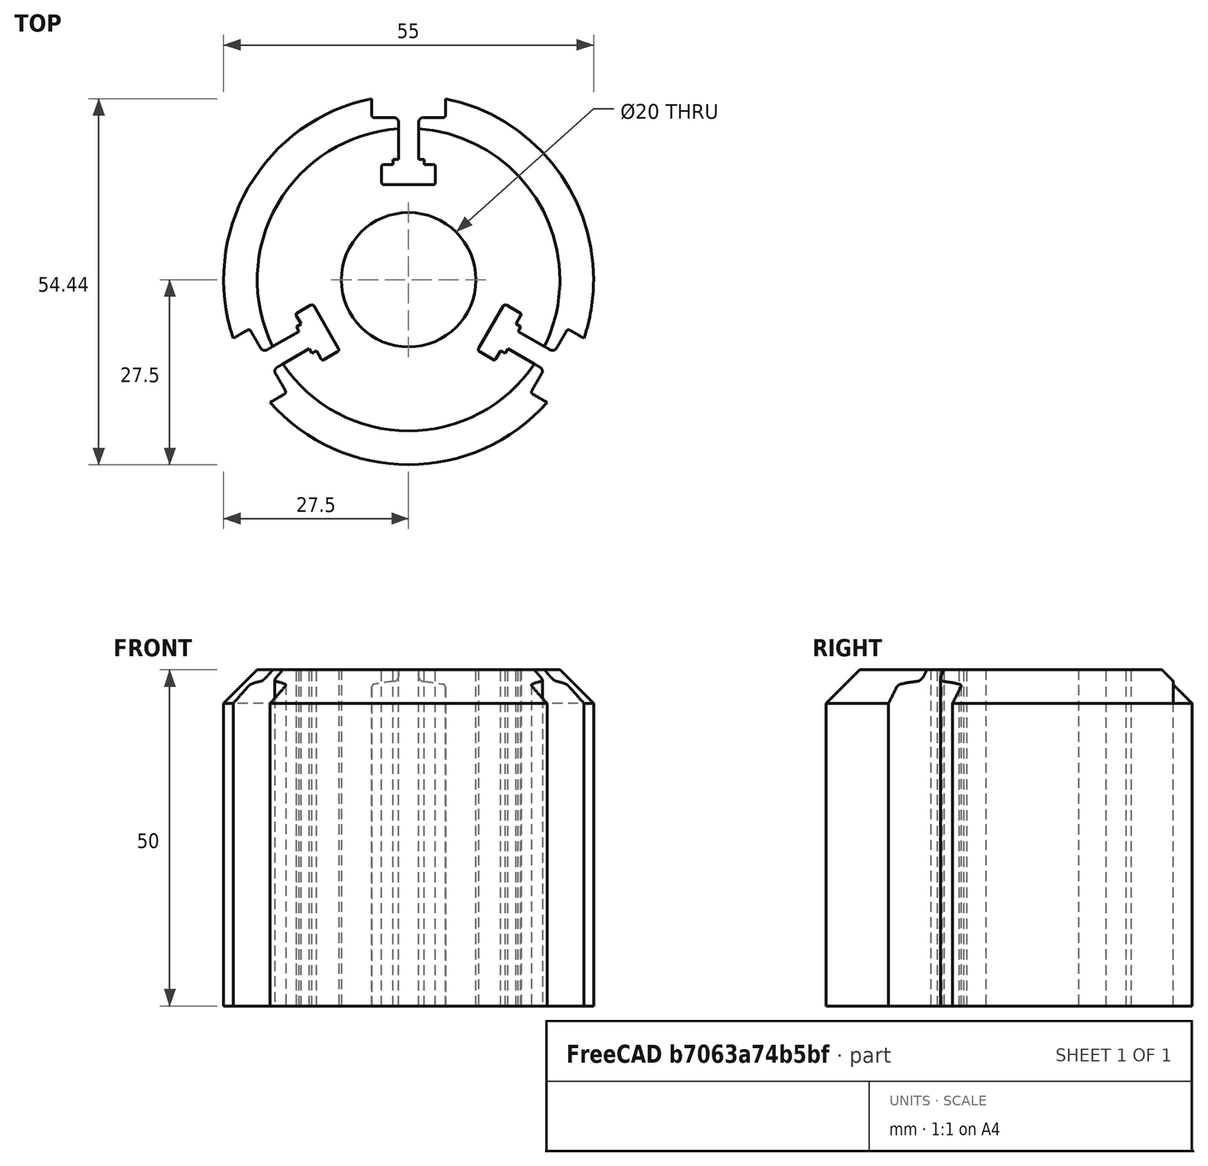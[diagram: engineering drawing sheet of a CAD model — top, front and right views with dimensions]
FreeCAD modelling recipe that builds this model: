
FCSTD DOCUMENT  (FreeCAD 0.21R33771 (Git))
Label: SoportePino
License: All rights reserved
LicenseURL: http://en.wikipedia.org/wiki/All_rights_reserved
objects: Sketcher::SketchObject×2, PartDesign::Pad×1, PartDesign::Chamfer×1, PartDesign::Pocket×1, PartDesign::Body×1
note: 9 computed .brp shape members not serialized (recipe doc carries the construction recipe); baked Part::Feature solids carry a one-line shape summary decoded from their .brp

FEATURE [Sketcher::SketchObject] Sketch
  FullyConstrained = true
  MapMode = 5
  sketch-geometry (2):
    g0: Circle CenterX=0 CenterY=0 CenterZ=0 NormalX=0 NormalY=0 NormalZ=1 AngleXU=0 Radius=27.5
    g1: Circle CenterX=0 CenterY=0 CenterZ=0 NormalX=0 NormalY=0 NormalZ=1 AngleXU=0 Radius=10
  constraints (4):
    c: Diameter(g0) = 55
    c: Coincident(g0,g-1)
    c: Diameter(g1) = 20
    c: Coincident(g1,g0)
FEATURE [PartDesign::Pad] Pad
  Direction = (0,0,1)
  Length = 50
  Length2 = 10
  Profile = -> Sketch
  ReferenceAxis = -> Sketch [N_Axis]
  Type = 0
FEATURE [PartDesign::Chamfer] Chamfer
  Angle = 45
  Base = -> Pad [Edge3]
  BaseFeature = -> Pad
  ChamferType = 0
  FlipDirection = false
  Size = 5
  Size2 = 1
  SupportTransform = false
  UseAllEdges = false
FEATURE [Sketcher::SketchObject] Sketch001
  FullyConstrained = false
  MapMode = 5
  Placement = pos=(0,0,0) rot=(1,0,0;3.14159rad)
  sketch-geometry (108):
    g0: LineSegment StartX=5.5 StartY=-27.8836 StartZ=0 EndX=5.5 EndY=-24.5112 EndZ=0
    g1: LineSegment StartX=5.10884 StartY=-24.12 StartZ=0 EndX=2.18624 EndY=-24.12 EndZ=0
    g2: LineSegment StartX=-1e-16 StartY=-24.12 StartZ=0 EndX=1.5 EndY=-24.12 EndZ=0
    g3: LineSegment StartX=1.5 StartY=-23.4338 StartZ=0 EndX=1.5 EndY=-17.927 EndZ=0
    g4: LineSegment StartX=4 StartY=-16.8721 StartZ=0 EndX=4 EndY=-14.489 EndZ=0
    g5: ArcOfCircle CenterX=2.18624 CenterY=-23.4338 CenterZ=0 NormalX=0 NormalY=0 NormalZ=1 AngleXU=0 Radius=0.686238 StartAngle=3.14159 EndAngle=4.71239
    g6: GeomPoint X=1.5 Y=-17.12 Z=0
    g7: ArcOfCircle CenterX=3.63103 CenterY=-14.489 CenterZ=0 NormalX=0 NormalY=0 NormalZ=1 AngleXU=0 Radius=0.368966 StartAngle=0 EndAngle=1.5708
    g8: GeomPoint X=4 Y=-14.12 Z=0
    g9: ArcOfCircle CenterX=3.75214 CenterY=-16.8721 CenterZ=0 NormalX=0 NormalY=0 NormalZ=1 AngleXU=0 Radius=0.247857 StartAngle=4.71239 EndAngle=6.28319
    g10: GeomPoint X=4 Y=-17.12 Z=0
    g11: ArcOfCircle CenterX=5.10884 CenterY=-24.5112 CenterZ=0 NormalX=0 NormalY=0 NormalZ=1 AngleXU=0 Radius=0.391159 StartAngle=0 EndAngle=1.5708
    g12: GeomPoint X=5.5 Y=-24.12 Z=0
    g13: LineSegment StartX=0 StartY=-25.1224 StartZ=0 EndX=1.5 EndY=-25.1224 EndZ=0
    g14: LineSegment StartX=2.29402 StartY=-17.927 StartZ=0 EndX=2.29402 EndY=-17.12 EndZ=0
    g15: LineSegment StartX=-5.5 StartY=-27.8836 StartZ=0 EndX=-5.5 EndY=-24.5112 EndZ=0
    g16: LineSegment StartX=-5.10884 StartY=-24.12 StartZ=0 EndX=-2.18624 EndY=-24.12 EndZ=0
    g17: LineSegment StartX=1e-16 StartY=-24.12 StartZ=0 EndX=-1.5 EndY=-24.12 EndZ=0
    g18: LineSegment StartX=-1.5 StartY=-23.4338 StartZ=0 EndX=-1.5 EndY=-17.927 EndZ=0
    g19: LineSegment StartX=-4 StartY=-16.8721 StartZ=0 EndX=-4 EndY=-14.489 EndZ=0
    g20: ArcOfCircle CenterX=-2.18624 CenterY=-23.4338 CenterZ=0 NormalX=0 NormalY=0 NormalZ=1 AngleXU=0 Radius=0.686238 StartAngle=4.71239 EndAngle=6.28319
    g21: GeomPoint X=-1.5 Y=-17.12 Z=0
    g22: ArcOfCircle CenterX=-3.63103 CenterY=-14.489 CenterZ=0 NormalX=0 NormalY=0 NormalZ=1 AngleXU=0 Radius=0.368966 StartAngle=1.5708 EndAngle=3.14159
    g23: GeomPoint X=-4 Y=-14.12 Z=0
    g24: ArcOfCircle CenterX=-3.75214 CenterY=-16.8721 CenterZ=0 NormalX=0 NormalY=0 NormalZ=1 AngleXU=0 Radius=0.247857 StartAngle=3.14159 EndAngle=4.71239
    g25: GeomPoint X=-4 Y=-17.12 Z=0
    g26: ArcOfCircle CenterX=-5.10884 CenterY=-24.5112 CenterZ=0 NormalX=0 NormalY=0 NormalZ=1 AngleXU=0 Radius=0.391159 StartAngle=1.5708 EndAngle=3.14159
    g27: GeomPoint X=-5.5 Y=-24.12 Z=0
    g28: LineSegment StartX=0 StartY=-25.1224 StartZ=0 EndX=-1.5 EndY=-25.1224 EndZ=0
    g29: LineSegment StartX=-2.29402 StartY=-17.927 StartZ=0 EndX=-2.29402 EndY=-17.12 EndZ=0
    g30: LineSegment StartX=-5.5 StartY=-27.8836 StartZ=0 EndX=5.5 EndY=-27.8836 EndZ=0
    g31: LineSegment StartX=-2.29402 StartY=-17.927 StartZ=0 EndX=-1.5 EndY=-17.927 EndZ=0
    g32: LineSegment StartX=1.5 StartY=-17.927 StartZ=0 EndX=2.29402 EndY=-17.927 EndZ=0
    g33: LineSegment StartX=-3.75214 StartY=-17.12 StartZ=0 EndX=-2.29402 EndY=-17.12 EndZ=0
    g34: LineSegment StartX=2.29402 StartY=-17.12 StartZ=0 EndX=3.75214 EndY=-17.12 EndZ=0
    g35: LineSegment StartX=3.63103 StartY=-14.12 StartZ=0 EndX=-3.63103 EndY=-14.12 EndZ=0
    g36: LineSegment StartX=21.3979 StartY=18.7049 StartZ=0 EndX=18.4773 EndY=17.0187 EndZ=0
    g37: LineSegment StartX=18.3341 StartY=16.4844 StartZ=0 EndX=19.7954 EndY=13.9533 EndZ=0
    g38: LineSegment StartX=20.8885 StartY=12.06 StartZ=0 EndX=20.1385 EndY=13.359 EndZ=0
    g39: LineSegment StartX=19.5442 StartY=13.0159 StartZ=0 EndX=14.7752 EndY=10.2625 EndZ=0
    g40: LineSegment StartX=12.6117 StartY=11.9002 StartZ=0 EndX=10.5478 EndY=10.7086 EndZ=0
    g41: ArcOfCircle CenterX=19.2011 CenterY=13.6102 CenterZ=0 NormalX=0 NormalY=0 NormalZ=1 AngleXU=0 Radius=0.686238 StartAngle=5.23599 EndAngle=6.80678
    g42: GeomPoint X=14.0764 Y=9.85904 Z=0
    g43: ArcOfCircle CenterX=10.7323 CenterY=10.3891 CenterZ=0 NormalX=0 NormalY=0 NormalZ=1 AngleXU=0 Radius=0.368966 StartAngle=2.0944 EndAngle=3.66519
    g44: GeomPoint X=10.2283 Y=10.5241 Z=0
    g45: ArcOfCircle CenterX=12.7356 CenterY=11.6855 CenterZ=0 NormalX=0 NormalY=0 NormalZ=1 AngleXU=0 Radius=0.247857 StartAngle=0.523599 EndAngle=2.0944
    g46: GeomPoint X=12.8264 Y=12.0241 Z=0
    g47: ArcOfCircle CenterX=18.6729 CenterY=16.68 CenterZ=0 NormalX=0 NormalY=0 NormalZ=1 AngleXU=0 Radius=0.391159 StartAngle=2.09439 EndAngle=3.66519
    g48: GeomPoint X=18.1385 Y=16.8231 Z=0
    g49: LineSegment StartX=21.7567 StartY=12.5612 StartZ=0 EndX=21.0067 EndY=13.8603 EndZ=0
    g50: LineSegment StartX=14.3782 StartY=10.9502 StartZ=0 EndX=13.6793 EndY=10.5467 EndZ=0
    g51: LineSegment StartX=26.8979 StartY=9.17865 StartZ=0 EndX=23.9773 EndY=7.49244 EndZ=0
    g52: LineSegment StartX=23.443 StartY=7.63561 StartZ=0 EndX=21.9817 EndY=10.1667 EndZ=0
    g53: LineSegment StartX=20.8885 StartY=12.06 StartZ=0 EndX=21.6385 EndY=10.761 EndZ=0
    g54: LineSegment StartX=21.0442 StartY=10.4178 StartZ=0 EndX=16.2752 EndY=7.66444 EndZ=0
    g55: LineSegment StartX=16.6117 StartY=4.97197 StartZ=0 EndX=14.5478 EndY=3.78038 EndZ=0
    g56: ArcOfCircle CenterX=21.3874 CenterY=9.82354 CenterZ=0 NormalX=0 NormalY=0 NormalZ=1 AngleXU=0 Radius=0.686238 StartAngle=0.523599 EndAngle=2.0944
    g57: GeomPoint X=15.5764 Y=7.26096 Z=0
    g58: ArcOfCircle CenterX=14.3633 CenterY=4.09992 CenterZ=0 NormalX=0 NormalY=0 NormalZ=1 AngleXU=0 Radius=0.368966 StartAngle=3.66519 EndAngle=5.23599
    g59: GeomPoint X=14.2283 Y=3.5959 Z=0
    g60: ArcOfCircle CenterX=16.4878 CenterY=5.18662 CenterZ=0 NormalX=0 NormalY=0 NormalZ=1 AngleXU=0 Radius=0.247857 StartAngle=5.23599 EndAngle=6.80678
    g61: GeomPoint X=16.8264 Y=5.0959 Z=0
    g62: ArcOfCircle CenterX=23.7817 CenterY=7.83119 CenterZ=0 NormalX=0 NormalY=0 NormalZ=1 AngleXU=0 Radius=0.391159 StartAngle=3.66519 EndAngle=5.23599
    g63: GeomPoint X=23.6385 Y=7.29686 Z=0
    g64: LineSegment StartX=21.7567 StartY=12.5612 StartZ=0 EndX=22.5067 EndY=11.2622 EndZ=0
    g65: LineSegment StartX=16.6722 StartY=6.9768 StartZ=0 EndX=15.9734 EndY=6.57332 EndZ=0
    g66: LineSegment StartX=26.8979 StartY=9.17865 StartZ=0 EndX=21.3979 EndY=18.7049 EndZ=0
    g67: LineSegment StartX=16.6722 StartY=6.9768 StartZ=0 EndX=16.2752 EndY=7.66444 EndZ=0
    g68: LineSegment StartX=14.7752 StartY=10.2625 StartZ=0 EndX=14.3782 EndY=10.9502 EndZ=0
    g69: LineSegment StartX=16.7024 StartY=5.31055 StartZ=0 EndX=15.9734 EndY=6.57332 EndZ=0
    g70: LineSegment StartX=13.6793 StartY=10.5467 StartZ=0 EndX=12.9503 EndY=11.8095 EndZ=0
    g71: LineSegment StartX=10.4128 StartY=10.2046 StartZ=0 EndX=14.0438 EndY=3.91543 EndZ=0
    g72: LineSegment StartX=-26.8979 StartY=9.17865 StartZ=0 EndX=-23.9773 EndY=7.49244 EndZ=0
    g73: LineSegment StartX=-23.443 StartY=7.63561 StartZ=0 EndX=-21.9817 EndY=10.1667 EndZ=0
    g74: LineSegment StartX=-20.8885 StartY=12.06 StartZ=0 EndX=-21.6385 EndY=10.761 EndZ=0
    g75: LineSegment StartX=-21.0442 StartY=10.4178 StartZ=0 EndX=-16.2752 EndY=7.66444 EndZ=0
    g76: LineSegment StartX=-16.6117 StartY=4.97197 StartZ=0 EndX=-14.5478 EndY=3.78038 EndZ=0
    g77: ArcOfCircle CenterX=-21.3874 CenterY=9.82354 CenterZ=0 NormalX=0 NormalY=0 NormalZ=1 AngleXU=0 Radius=0.686238 StartAngle=1.0472 EndAngle=2.61799
    g78: GeomPoint X=-15.5764 Y=7.26096 Z=0
    g79: ArcOfCircle CenterX=-14.3633 CenterY=4.09992 CenterZ=0 NormalX=0 NormalY=0 NormalZ=1 AngleXU=0 Radius=0.368966 StartAngle=4.18879 EndAngle=5.75959
    g80: GeomPoint X=-14.2283 Y=3.5959 Z=0
    g81: ArcOfCircle CenterX=-16.4878 CenterY=5.18662 CenterZ=0 NormalX=0 NormalY=0 NormalZ=1 AngleXU=0 Radius=0.247857 StartAngle=2.61799 EndAngle=4.18879
    g82: GeomPoint X=-16.8264 Y=5.0959 Z=0
    g83: ArcOfCircle CenterX=-23.7817 CenterY=7.83119 CenterZ=0 NormalX=0 NormalY=0 NormalZ=1 AngleXU=0 Radius=0.391159 StartAngle=4.18879 EndAngle=5.75959
    g84: GeomPoint X=-23.6385 Y=7.29686 Z=0
    g85: LineSegment StartX=-21.7567 StartY=12.5612 StartZ=0 EndX=-22.5067 EndY=11.2622 EndZ=0
    g86: LineSegment StartX=-16.6722 StartY=6.9768 StartZ=0 EndX=-15.9734 EndY=6.57332 EndZ=0
    g87: LineSegment StartX=-21.3979 StartY=18.7049 StartZ=0 EndX=-18.4773 EndY=17.0187 EndZ=0
    g88: LineSegment StartX=-18.3341 StartY=16.4844 StartZ=0 EndX=-19.7954 EndY=13.9533 EndZ=0
    g89: LineSegment StartX=-20.8885 StartY=12.06 StartZ=0 EndX=-20.1385 EndY=13.359 EndZ=0
    g90: LineSegment StartX=-19.5442 StartY=13.0159 StartZ=0 EndX=-14.7752 EndY=10.2625 EndZ=0
    g91: LineSegment StartX=-12.6117 StartY=11.9002 StartZ=0 EndX=-10.5478 EndY=10.7086 EndZ=0
    g92: ArcOfCircle CenterX=-19.2011 CenterY=13.6102 CenterZ=0 NormalX=0 NormalY=0 NormalZ=1 AngleXU=0 Radius=0.686238 StartAngle=2.61799 EndAngle=4.18879
    g93: GeomPoint X=-14.0764 Y=9.85904 Z=0
    g94: ArcOfCircle CenterX=-10.7323 CenterY=10.3891 CenterZ=0 NormalX=0 NormalY=0 NormalZ=1 AngleXU=0 Radius=0.368966 StartAngle=5.75959 EndAngle=7.33038
    g95: GeomPoint X=-10.2283 Y=10.5241 Z=0
    g96: ArcOfCircle CenterX=-12.7356 CenterY=11.6855 CenterZ=0 NormalX=0 NormalY=0 NormalZ=1 AngleXU=0 Radius=0.247857 StartAngle=1.0472 EndAngle=2.61799
    g97: GeomPoint X=-12.8264 Y=12.0241 Z=0
    g98: ArcOfCircle CenterX=-18.6729 CenterY=16.68 CenterZ=0 NormalX=0 NormalY=0 NormalZ=1 AngleXU=0 Radius=0.391159 StartAngle=5.75959 EndAngle=7.33038
    g99: GeomPoint X=-18.1385 Y=16.8231 Z=0
    g100: LineSegment StartX=-21.7567 StartY=12.5612 StartZ=0 EndX=-21.0067 EndY=13.8603 EndZ=0
    g101: LineSegment StartX=-14.3782 StartY=10.9502 StartZ=0 EndX=-13.6793 EndY=10.5467 EndZ=0
    g102: LineSegment StartX=-21.3979 StartY=18.7049 StartZ=0 EndX=-26.8979 EndY=9.17865 EndZ=0
    g103: LineSegment StartX=-14.3782 StartY=10.9502 StartZ=0 EndX=-14.7752 EndY=10.2625 EndZ=0
    g104: LineSegment StartX=-16.2752 StartY=7.66444 StartZ=0 EndX=-16.6722 EndY=6.9768 EndZ=0
    g105: LineSegment StartX=-12.9503 StartY=11.8095 StartZ=0 EndX=-13.6793 EndY=10.5467 EndZ=0
    g106: LineSegment StartX=-15.9734 StartY=6.57332 StartZ=0 EndX=-16.7024 EndY=5.31055 EndZ=0
    g107: LineSegment StartX=-14.0438 StartY=3.91543 StartZ=0 EndX=-10.4128 EndY=10.2046 EndZ=0
  constraints (128):
    c: Horizontal(g1)
    c: Vertical(g0)
    c: Horizontal(g2)
    c: Vertical(g3)
    c: Vertical(g4)
    c: Distance(g10,g8) = 3
    c: Tangent(g3,g5) = 1.5708
    c: Tangent(g1,g5) = 1.5708
    c: PointOnObject(g6,g3)
    c: PointOnObject(g8,g4)
    c: Tangent(g4,g7) = -1.5708
    c: PointOnObject(g10,g4)
    c: Tangent(g4,g9) = -1.5708
    c: PointOnObject(g12,g1)
    c: PointOnObject(g12,g0)
    c: Tangent(g1,g11) = -1.5708
    c: Tangent(g0,g11) = -1.5708
    c: Horizontal(g13)
    c: Vertical(g14)
    c: Horizontal(g16)
    c: Vertical(g15)
    c: Horizontal(g17)
    c: Vertical(g18)
    c: Vertical(g19)
    c: Distance(g25,g23) = 3
    c: Tangent(g18,g20) = -1.5708
    c: Tangent(g16,g20) = -1.5708
    c: PointOnObject(g21,g18)
    c: PointOnObject(g23,g19)
    c: Tangent(g19,g22) = 1.5708
    c: PointOnObject(g25,g19)
    c: Tangent(g19,g24) = 1.5708
    c: PointOnObject(g27,g16)
    c: PointOnObject(g27,g15)
    c: Tangent(g16,g26) = 1.5708
    c: Tangent(g15,g26) = 1.5708
    c: Horizontal(g28)
    c: Vertical(g29)
    c: Coincident(g30,g15)
    c: Coincident(g30,g0)
    c: Horizontal(g30)
    c: Coincident(g31,g29)
    c: Coincident(g31,g18)
    c: Horizontal(g31)
    c: Coincident(g32,g3)
    c: Coincident(g32,g14)
    c: Horizontal(g32)
    c: Tangent(g33,g24) = -1.5708
    c: Coincident(g33,g29)
    c: Horizontal(g33)
    c: Coincident(g34,g14)
    c: Tangent(g34,g9) = -1.5708
    c: Horizontal(g34)
    c: Tangent(g35,g7) = -1.5708
    c: Coincident(g35,g22)
    c: Horizontal(g35)
    c: Distance(g46,g44) = 3
    c: Distance(g82,g80) = 3
    c: Tangent(g39,g41) = 1.5708
    c: Tangent(g75,g77) = 1.5708
    c: Tangent(g37,g41) = 1.5708
    c: Tangent(g73,g77) = 1.5708
    c: PointOnObject(g42,g39)
    c: PointOnObject(g78,g75)
    c: PointOnObject(g44,g40)
    c: PointOnObject(g80,g76)
    c: Tangent(g40,g43) = -1.5708
    c: Tangent(g76,g79) = -1.5708
    c: PointOnObject(g46,g40)
    c: PointOnObject(g82,g76)
    c: Tangent(g40,g45) = -1.5708
    c: Tangent(g76,g81) = -1.5708
    c: PointOnObject(g48,g37)
    c: PointOnObject(g84,g73)
    c: PointOnObject(g48,g36)
    c: PointOnObject(g84,g72)
    c: Tangent(g37,g47) = -1.5708
    c: Tangent(g73,g83) = -1.5708
    c: Tangent(g36,g47) = -1.5708
    c: Tangent(g72,g83) = -1.5708
    c: Distance(g61,g59) = 3
    c: Distance(g97,g95) = 3
    c: Tangent(g54,g56) = -1.5708
    c: Tangent(g90,g92) = -1.5708
    c: Tangent(g52,g56) = -1.5708
    c: Tangent(g88,g92) = -1.5708
    c: PointOnObject(g57,g54)
    c: PointOnObject(g93,g90)
    c: PointOnObject(g59,g55)
    c: PointOnObject(g95,g91)
    c: Tangent(g55,g58) = 1.5708
    c: Tangent(g91,g94) = 1.5708
    c: PointOnObject(g61,g55)
    c: PointOnObject(g97,g91)
    c: Tangent(g55,g60) = 1.5708
    c: Tangent(g91,g96) = 1.5708
    c: PointOnObject(g63,g52)
    c: PointOnObject(g99,g88)
    c: PointOnObject(g63,g51)
    c: PointOnObject(g99,g87)
    c: Tangent(g52,g62) = 1.5708
    c: Tangent(g88,g98) = 1.5708
    c: Tangent(g51,g62) = 1.5708
    c: Tangent(g87,g98) = 1.5708
    c: Coincident(g66,g51)
    c: Coincident(g102,g87)
    c: Coincident(g66,g36)
    c: Coincident(g102,g72)
    c: Coincident(g67,g65)
    c: Coincident(g103,g101)
    c: Coincident(g67,g54)
    c: Coincident(g103,g90)
    c: Coincident(g68,g39)
    c: Coincident(g104,g75)
    c: Coincident(g68,g50)
    c: Coincident(g104,g86)
    c: Tangent(g69,g60) = -1.5708
    c: Tangent(g105,g96) = -1.5708
    c: Coincident(g69,g65)
    c: Coincident(g105,g101)
    c: Coincident(g70,g50)
    c: Coincident(g106,g86)
    c: Tangent(g70,g45) = -1.5708
    c: Tangent(g106,g81) = -1.5708
    c: Tangent(g71,g43) = -1.5708
    c: Tangent(g107,g79) = -1.5708
    c: Coincident(g71,g58)
    c: Coincident(g107,g94)
FEATURE [PartDesign::Pocket] Pocket
  BaseFeature = -> Chamfer
  Direction = (0,0,1)
  Length = 5
  Length2 = 5
  Profile = -> Sketch001
  ReferenceAxis = -> Sketch001 [N_Axis]
  Type = 1
FEATURE [PartDesign::Body] Body
  Group = -> [Sketch,Pad,Chamfer,Sketch001,Pocket]
  Origin = -> Origin
  Tip = -> Pocket
